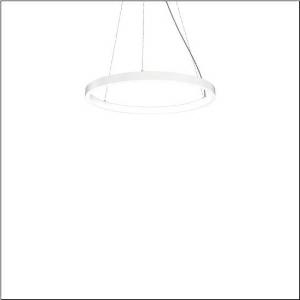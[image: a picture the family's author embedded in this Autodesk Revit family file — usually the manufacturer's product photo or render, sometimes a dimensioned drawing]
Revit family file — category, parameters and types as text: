
# Revit family: silica_21_ring-i_5pjbi2d1004a
name_source: partatom
category: Lighting Fixtures
units: mm (PartAtom-declared; Revit-internal decimal feet)

## family parameters
Cut with Voids When Loaded = No
Host = Face
Light Source = No
Part Type = Normal
Room Calculation Point = No
Round Connector Dimension = Use Diameter
Shared = No

## types (1)
- Silica 21 Ring-I (1 x LED, 4800 lm, 80 W, 3000K)
    Apparent Load = 80 VA
    CIE Flux Codes = 22 48 76 50 101
    Color Rendering = 80
    Color Temperature = 3000K
    Default Elevation = 1800 mm
    Description = Silica 21 Ring-I, suspended luminaire, of PMMA, frosted, light emission: inner ring side luminous distribution, primary light characteristic: symmetric, installation type: suspended mounting, LED, rated luminous flux: 4.800lm, luminous efficacy: 60lm/W, light colour: 830, colour temperature: 3000K, control gear: DALI 2, with terminal, 5-pole, mains connection: 230V, AC/DC, 0/50..60Hz, rated input power: 80W, housing, of extruded aluminium section, traffic white (RAL 9016), diameter: 805mm, ceiling canopy, traffic white (RAL 9016), protection rating (lamp compartment): IP40, insulation class (complete): insulation class I (protective earthing), certification: CE, impact resistance: IK02, permissible operating ambient temperature: 0..+35°C, packaging unit: 1 piece
    Height = 48 mm  [stored 0.15748 ft]
    Lamp = 1 x LED
    Lamp Light Flux = 4800 lm
    Lamp Power = 80 W
    Lamp count = 1
    Length = 805 mm
    Luminous efficacy = 60 lm/W
    Manufacturer = Siteco
    ModVariant = No
    Model = 5PJBI2D1004A
    Mounting Place = Ceiling
    Mounting Type = Pendant
    Number of Poles = 1
    OnlyDefault = Yes
    Power Factor = 1
    Product Name = Silica 21 Ring-I
    Product group = suspended luminaire
    ProductGroupID = 904
    Protection Class = Protection class I
    Protection Degree = IP 40
    RLX_Detail_Level = 1
    RLX_Emergency_Light_Flux = 0 lm
    RLX_Emergency_Type = 0
    RLX_Emergency_Type_DB = No
    RlxData = <blob elided: 11565 chars, md5=f28372ce>
    Socket = socket
    Standby Power = 0 W
    System Light Flux = 4800 lm
    System Power = 80 W
    Type Comments = Product without accessories
    Type Image = l_1258367.jpg
    URL = http://relux.com
    VarID = ---
    Voltage = 0 V
    Weight = 0.00 kg
    Width = 0 mm  [stored 0 ft]

note: [stored X ft] marks values corroborated as IEEE doubles in the binary element streams (Revit-internal decimal feet)

## geometry (parser evidence)
native form markers: Sweep x11
no freeform markers — native parametric forms only
